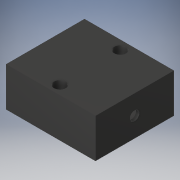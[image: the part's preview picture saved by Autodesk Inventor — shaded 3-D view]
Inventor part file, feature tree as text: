
AUTODESK INVENTOR PART (.ipt)
format: ipt  version: 2018 (Build 220112000, 112)  size: 121,344 bytes
history: native  units: in
note: dims shown in document units (in); Inventor stores cm internally (conversion verified against a paired STEP export)
features: extrude x3, sketch x3, hole x1
ambient origin geometry x8: Origin, YZ Plane, XZ Plane, XY Plane, X Axis, Y Axis, Z Axis, Center Point
bodies: Solid1 (feature_tree)
feature tree (7):
  extrude  "Extrusion1"  Depth=1.0in
  hole  "Hole1"  [1 undecoded]
  extrude  "Extrusion3"  Depth=1.1in
  extrude  "Extrusion5"  Depth=1.1in
  sketch  "Sketch1"  dims[d0=1.14in d1=1.0in]
  sketch  "Sketch2"  dims[d2=0.5in d3=0.0in d4=0.385in]
  sketch  "Sketch5"  dims[d5=0.77in d6=0.15in d7=0.75in d8=0.279in d9=0.093in d10=0.5635in d11=1.0in d12=0.8108in d13=0.1181in d14=0.25in d15=0.5in d19=0.3819in d20=0.0in d23=0.48in d24=0.4in d25=0.05in d26=0.05in d27=1.1in d28=0.0in]
note: 1 required parameter value undecoded (feature->parameter linkage not recoverable at this tier; creation-order binding heuristic only, values carry confidence <= 0.55)
